# Revit family: QF_MACOM_FR71_N-G
name_source: partatom
category: Equipamento especial
units: mm (PartAtom-declared; Revit-internal decimal feet)

## family parameters
Com base no plano de trabalho = Não
Compartilhado = Não
Corte com vazios quando carregada = Não
Cota do conector redondo = Utilizar diâmetro
Número OmniClass = 23.40.40.14.17.11
Ponto de cálculo do ambiente = Não
Sempre na vertical = Sim
Tipo de parte = Normal
Título OmniClass = Cookers, Ovens, Stoves

## types (2) — shared parameters
Cooking Capacity = 25,0 L
Cycle = 60 Hz
Depth = 745 mm
Descrição = FRIGIDEIRA BASCULANTE MACOM 25 LITROS
Electric Power = 100 W
Elevação padrão = 0 mm
Fabricante = MACOM
Fryning Capacity = 9,0 L
Gas Connection Height = 56 mm
Gas Size = 3/4"
Height = 614 mm
Phase (text) = 1 or 2
Show Clearances = Sim
URL = https://www.acosmacom.com.br
Volts = 220 V
Volume = 0,24 m³
Weight = 60,00 kg
Width = 540 mm

## per-type parameters (varying)
| type | Elec Connection Height | Gas Consumption GLP | Gas Consumption GN | Gas Input GLP | Gas Input GN | Gas Pressure |
| FR71-G | 15 mm | 0,82 Kg/h | 0 m³/h | 37255 Btu/h |  | 0,03 bar |
| FR71-N | 0 mm |  | 1 m³/h | 0 Btu/h | 9389 Kcal/h | 0,02 bar |

note: column(s) folded — value = type name in every type: Modelo

## geometry (parser evidence)
native form markers: Sweep x8
no freeform markers — native parametric forms only
